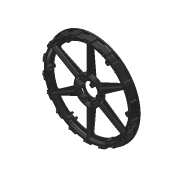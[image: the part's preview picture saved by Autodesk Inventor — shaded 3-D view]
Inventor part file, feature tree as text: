
AUTODESK INVENTOR PART (.ipt)
format: ipt  version: 2013 (Build 170138000, 138)  size: 2,206,208 bytes
history: native  units: in
note: dims shown in document units (in); Inventor stores cm internally (conversion verified against a paired STEP export)
features: chamfer x1, other x1, imported_body x1
ambient origin geometry x8: Origin, YZ Plane, XZ Plane, XY Plane, X Axis, Y Axis, Z Axis, Center Point
feature tree (3):
  chamfer  "Chamfer1"  [1 undecoded]
  other  "217-2605-001 Rev11"
  imported_body  "Base1"
note: 1 required parameter value undecoded (feature->parameter linkage not recoverable at this tier; creation-order binding heuristic only, values carry confidence <= 0.55)
